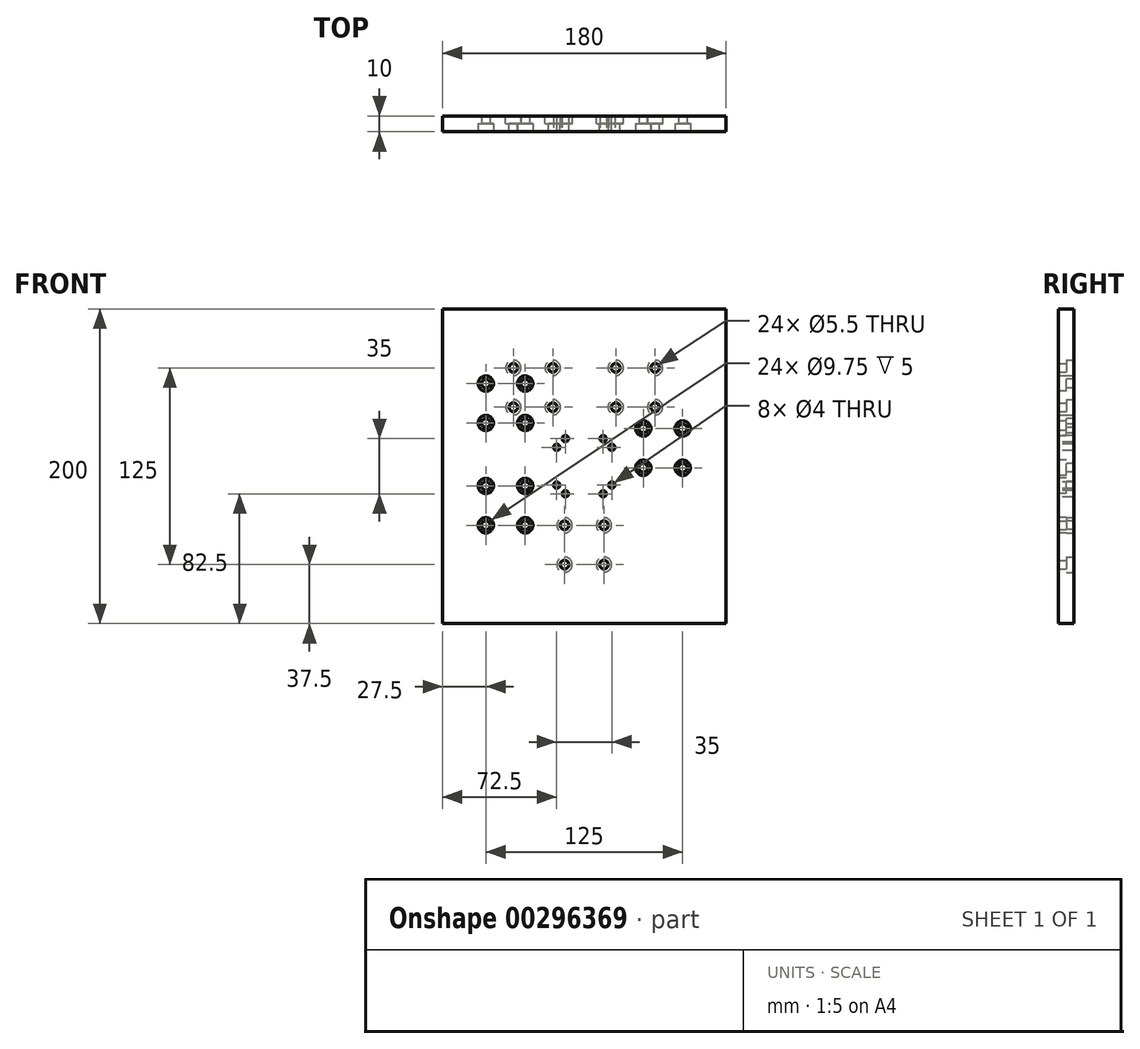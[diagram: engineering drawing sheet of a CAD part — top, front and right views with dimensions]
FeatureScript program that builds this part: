
annotation { "Feature Type Name" : "Feature", "Feature Type Description" : "" }
export const myFeature = defineFeature(function(context is Context, id is Id, definition is map)
    precondition{}
    {
        {
            var Q0;
            Q0=qCreatedBy(makeId("Front.planeOp"),FACE);
            var sketch = newSketch(context, id + "F0", { "sketchPlane" : qUnion([Q0])});
            skLineSegment(sketch, "E0.bottom", {"start": v(90, 100) * mm, "end": v(-90, 100) * mm});
            skLineSegment(sketch, "E0.top", {"start": v(90, -100) * mm, "end": v(-90, -100) * mm});
            skLineSegment(sketch, "E0.left", {"start": v(90, 100) * mm, "end": v(90, -100) * mm});
            skLineSegment(sketch, "E0.right", {"start": v(-90, 100) * mm, "end": v(-90, -100) * mm});
            skPoint(sketch, "E0.middle", {"position": v(0, 0) * mm});
            skLineSegment(sketch, "E1", {"start": v(-90, 50) * mm, "end": v(90, 50) * mm, "construction": true});
            skLineSegment(sketch, "E2", {"start": v(-90, 0) * mm, "end": v(90, 0) * mm, "construction": true});
            skLineSegment(sketch, "E3", {"start": v(-90, -50) * mm, "end": v(90, -50) * mm, "construction": true});
            skLineSegment(sketch, "E4", {"start": v(-32.5, 100) * mm, "end": v(-32.5, 0) * mm, "construction": true});
            skLineSegment(sketch, "E5", {"start": v(0, 100) * mm, "end": v(0, -100) * mm, "construction": true});
            skLineSegment(sketch, "E6", {"start": v(32.5, 100) * mm, "end": v(32.5, 0) * mm, "construction": true});
            skLineSegment(sketch, "E7.0", {"start": v(-45, 60) * mm, "end": v(-45, 0) * mm, "construction": true});
            skLineSegment(sketch, "E8.0", {"start": v(-20, 60) * mm, "end": v(-20, 0) * mm, "construction": true});
            skLineSegment(sketch, "E9.0", {"start": v(20, 60) * mm, "end": v(20, 0) * mm, "construction": true});
            skLineSegment(sketch, "E10.0", {"start": v(45, 60) * mm, "end": v(45, 0) * mm, "construction": true});
            skLineSegment(sketch, "E11.0", {"start": v(-60, 37.5) * mm, "end": v(60, 37.5) * mm, "construction": true});
            skLineSegment(sketch, "E12.0", {"start": v(-60, 62.5) * mm, "end": v(60, 62.5) * mm, "construction": true});
            skLineSegment(sketch, "E13.0", {"start": v(-60, -62.5) * mm, "end": v(60, -62.5) * mm, "construction": true});
            skLineSegment(sketch, "E14.0", {"start": v(-60, -37.5) * mm, "end": v(60, -37.5) * mm, "construction": true});
            skLineSegment(sketch, "E15.trimOffspring", {"start": v(12.5, 0) * mm, "end": v(12.5, -100) * mm, "construction": true});
            skLineSegment(sketch, "E16.trimOffspring", {"start": v(-12.5, 0) * mm, "end": v(-12.5, -100) * mm, "construction": true});
            skPoint(sketch, "E17", {"position": v(-45, 62.5) * mm});
            skPoint(sketch, "E18", {"position": v(-45, 37.5) * mm});
            skPoint(sketch, "E19", {"position": v(-20, 37.5) * mm});
            skPoint(sketch, "E20", {"position": v(-20, 62.5) * mm});
            skPoint(sketch, "E21", {"position": v(20, 62.5) * mm});
            skPoint(sketch, "E22", {"position": v(45, 62.5) * mm});
            skPoint(sketch, "E23", {"position": v(45, 37.5) * mm});
            skPoint(sketch, "E24", {"position": v(20, 37.5) * mm});
            skPoint(sketch, "E25", {"position": v(-12.5, -37.5) * mm});
            skPoint(sketch, "E26", {"position": v(12.5, -37.5) * mm});
            skPoint(sketch, "E27", {"position": v(12.5, -62.5) * mm});
            skPoint(sketch, "E28", {"position": v(-12.5, -62.5) * mm});
            skSolve(sketch);
        }
        {
            var Q0;
            Q0 = qSketchRegion(id + "F0", true);
            extrude(context, id + "F1", {"entities" : qUnion([Q0]), "depth" : 10 * mm});
        }
        {
            var Q0;
            Q0=sQuery(id+"F0.wireOp",VERTEX,"E17");
            var Q1;
            Q1=sQuery(id+"F0.wireOp",VERTEX,"E20");
            var Q2;
            Q2=sQuery(id+"F0.wireOp",VERTEX,"E19");
            var Q3;
            Q3=sQuery(id+"F0.wireOp",VERTEX,"E18");
            var Q4;
            Q4=sQuery(id+"F0.wireOp",VERTEX,"E21");
            var Q5;
            Q5=sQuery(id+"F0.wireOp",VERTEX,"E22");
            var Q6;
            Q6=sQuery(id+"F0.wireOp",VERTEX,"E23");
            var Q7;
            Q7=sQuery(id+"F0.wireOp",VERTEX,"E24");
            var Q8;
            Q8=sQuery(id+"F0.wireOp",VERTEX,"E26");
            var Q9;
            Q9=sQuery(id+"F0.wireOp",VERTEX,"E25");
            var Q10;
            Q10=sQuery(id+"F0.wireOp",VERTEX,"E28");
            var Q11;
            Q11=sQuery(id+"F0.wireOp",VERTEX,"E27");
            var Q12;
            Q12=makeQuery(id+"F1.opExtrude","SWEPT_BODY",BODY,{"disambiguationData":[OSD([sQuery(id+"F0.wireOp",EDGE,"E0.bottom"),sQuery(id+"F0.wireOp",EDGE,"E0.top"),sQuery(id+"F0.wireOp",EDGE,"E0.left"),sQuery(id+"F0.wireOp",EDGE,"E0.right")])]});
            hole(context, id + "F2", {"style" : HoleStyle.C_BORE, "endStyle" : HoleEndStyle.THROUGH, "oppositeDirection" : true, "standardTappedOrClearance" : lookupTablePath({ "standard" : "ISO", "fit" : "Normal", "size" : "M5", "type" : "Clearance" }), "standardBlindInLast" : lookupTablePath({ "fit" : "Standard", "standard" : "ISO", "size" : "M5", "type" : "Clearance" }), "holeDiameter" : 5.5 * mm, "cBoreDiameter" : 9.75 * mm, "cBoreDepth" : 5 * mm, "tappedDepth" : 8 * mm, "tapClearance" : 3, "locations" : qUnion([Q0, Q1, Q2, Q3, Q4, Q5, Q6, Q7, Q8, Q9, Q10, Q11]), "scope" : qUnion([Q12])});
        }
        {
            var Q0;
            Q0=makeQuery(id+"F1.opExtrude","CAP_FACE",FACE,{"disambiguationData":[OSD([sQuery(id+"F0.wireOp",EDGE,"E0.bottom"),sQuery(id+"F0.wireOp",EDGE,"E0.top"),sQuery(id+"F0.wireOp",EDGE,"E0.left"),sQuery(id+"F0.wireOp",EDGE,"E0.right")])],"isStart":false});
            var sketch = newSketch(context, id + "F3", { "sketchPlane" : qUnion([Q0])});
            skLineSegment(sketch, "E29", {"start": v(-50, -100) * mm, "end": v(-50, 100) * mm, "construction": true});
            skLineSegment(sketch, "E30", {"start": v(50, -19.94) * mm, "end": v(50, 100) * mm, "construction": true});
            skLineSegment(sketch, "E31", {"start": v(-90, 0) * mm, "end": v(90, 0) * mm, "construction": true});
            skLineSegment(sketch, "E32", {"start": v(0, -100) * mm, "end": v(0, 100) * mm, "construction": true});
            skLineSegment(sketch, "E33", {"start": v(-90, -25) * mm, "end": v(-10.57, -25) * mm, "construction": true});
            skLineSegment(sketch, "E34", {"start": v(-90, 40) * mm, "end": v(0, 40) * mm, "construction": true});
            skLineSegment(sketch, "E35.0", {"start": v(-60, -37.5) * mm, "end": v(-9.77, -37.5) * mm, "construction": true});
            skLineSegment(sketch, "E36.0", {"start": v(-60, -12.5) * mm, "end": v(-9.77, -12.5) * mm, "construction": true});
            skLineSegment(sketch, "E37.0", {"start": v(-60, 52.5) * mm, "end": v(2.2, 52.5) * mm, "construction": true});
            skLineSegment(sketch, "E38.0", {"start": v(-60, 27.5) * mm, "end": v(0, 27.5) * mm, "construction": true});
            skLineSegment(sketch, "E39.0", {"start": v(62.5, -19.94) * mm, "end": v(62.5, 60) * mm, "construction": true});
            skLineSegment(sketch, "E40.0", {"start": v(37.5, -19.94) * mm, "end": v(37.5, 60) * mm, "construction": true});
            skLineSegment(sketch, "E41.0", {"start": v(-37.5, -60) * mm, "end": v(-37.5, 60) * mm, "construction": true});
            skLineSegment(sketch, "E42.0", {"start": v(-62.5, -60) * mm, "end": v(-62.5, 60) * mm, "construction": true});
            skLineSegment(sketch, "E43.0", {"start": v(-60, 24) * mm, "end": v(60, 24) * mm, "construction": true});
            skLineSegment(sketch, "E44.0", {"start": v(-60, -1) * mm, "end": v(60, -1) * mm, "construction": true});
            skPoint(sketch, "E45", {"position": v(-62.5, -37.5) * mm});
            skPoint(sketch, "E46", {"position": v(-37.5, -37.5) * mm});
            skPoint(sketch, "E47", {"position": v(-37.5, -12.5) * mm});
            skPoint(sketch, "E48", {"position": v(-62.5, -12.5) * mm});
            skPoint(sketch, "E49", {"position": v(-62.5, 52.5) * mm});
            skPoint(sketch, "E50", {"position": v(-37.5, 52.5) * mm});
            skPoint(sketch, "E51", {"position": v(-37.5, 27.5) * mm});
            skPoint(sketch, "E52", {"position": v(-62.5, 27.5) * mm});
            skPoint(sketch, "E53", {"position": v(37.5, -1) * mm});
            skPoint(sketch, "E54", {"position": v(37.5, 24) * mm});
            skPoint(sketch, "E55", {"position": v(62.5, 24) * mm});
            skPoint(sketch, "E56", {"position": v(62.5, -1) * mm});
            skSolve(sketch);
        }
        {
            var Q0;
            Q0=sQuery(id+"F3.wireOp",VERTEX,"E45");
            var Q1;
            Q1=sQuery(id+"F3.wireOp",VERTEX,"E48");
            var Q2;
            Q2=sQuery(id+"F3.wireOp",VERTEX,"E47");
            var Q3;
            Q3=sQuery(id+"F3.wireOp",VERTEX,"E46");
            var Q4;
            Q4=sQuery(id+"F3.wireOp",VERTEX,"E52");
            var Q5;
            Q5=sQuery(id+"F3.wireOp",VERTEX,"E49");
            var Q6;
            Q6=sQuery(id+"F3.wireOp",VERTEX,"E50");
            var Q7;
            Q7=sQuery(id+"F3.wireOp",VERTEX,"E51");
            var Q8;
            Q8=sQuery(id+"F3.wireOp",VERTEX,"E53");
            var Q9;
            Q9=sQuery(id+"F3.wireOp",VERTEX,"E54");
            var Q10;
            Q10=sQuery(id+"F3.wireOp",VERTEX,"E55");
            var Q11;
            Q11=sQuery(id+"F3.wireOp",VERTEX,"E56");
            var Q12;
            Q12=makeQuery(id+"F1.opExtrude","SWEPT_BODY",BODY,{"disambiguationData":[OSD([sQuery(id+"F0.wireOp",EDGE,"E0.bottom"),sQuery(id+"F0.wireOp",EDGE,"E0.top"),sQuery(id+"F0.wireOp",EDGE,"E0.left"),sQuery(id+"F0.wireOp",EDGE,"E0.right")])]});
            hole(context, id + "F4", {"style" : HoleStyle.C_BORE, "endStyle" : HoleEndStyle.THROUGH, "standardTappedOrClearance" : lookupTablePath({ "standard" : "ISO", "fit" : "Normal", "size" : "M5", "type" : "Clearance" }), "standardBlindInLast" : lookupTablePath({ "fit" : "Standard", "standard" : "ISO", "size" : "M5", "type" : "Clearance" }), "holeDiameter" : 5.5 * mm, "cBoreDiameter" : 9.75 * mm, "cBoreDepth" : 5 * mm, "tappedDepth" : 8 * mm, "tapClearance" : 3, "locations" : qUnion([Q0, Q1, Q2, Q3, Q4, Q5, Q6, Q7, Q8, Q9, Q10, Q11]), "scope" : qUnion([Q12])});
        }
        {
            var Q0;
            Q0=makeQuery(id+"F1.opExtrude","CAP_FACE",FACE,{"disambiguationData":[OSD([sQuery(id+"F0.wireOp",EDGE,"E0.bottom"),sQuery(id+"F0.wireOp",EDGE,"E0.top"),sQuery(id+"F0.wireOp",EDGE,"E0.left"),sQuery(id+"F0.wireOp",EDGE,"E0.right")])],"isStart":false});
            var sketch = newSketch(context, id + "F5", { "sketchPlane" : qUnion([Q0])});
            skLineSegment(sketch, "E57", {"start": v(-62.5, 27.5) * mm, "end": v(-62.5, -12.5) * mm, "construction": true});
            skLineSegment(sketch, "E58", {"start": v(-17.5, 12) * mm, "end": v(-17.5, -12) * mm, "construction": true});
            skLineSegment(sketch, "E59", {"start": v(17.5, 12) * mm, "end": v(17.5, -12) * mm, "construction": true});
            skPoint(sketch, "E60", {"position": v(-17.5, 12) * mm});
            skPoint(sketch, "E61", {"position": v(-17.5, -12) * mm});
            skPoint(sketch, "E62", {"position": v(17.5, -12) * mm});
            skPoint(sketch, "E63", {"position": v(17.5, 12) * mm});
            skLineSegment(sketch, "E64", {"start": v(-20, 37.5) * mm, "end": v(20, 37.5) * mm, "construction": true});
            skLineSegment(sketch, "E65", {"start": v(-17.5, 12) * mm, "end": v(17.5, 12) * mm, "construction": true});
            skLineSegment(sketch, "E66", {"start": v(-17.5, -12) * mm, "end": v(17.5, -12) * mm, "construction": true});
            skLineSegment(sketch, "E67.bottom", {"start": v(-12, 17.5) * mm, "end": v(12, 17.5) * mm, "construction": true});
            skLineSegment(sketch, "E67.top", {"start": v(-12, -17.5) * mm, "end": v(12, -17.5) * mm, "construction": true});
            skLineSegment(sketch, "E67.left", {"start": v(-12, 17.5) * mm, "end": v(-12, -17.5) * mm, "construction": true});
            skLineSegment(sketch, "E67.right", {"start": v(12, 17.5) * mm, "end": v(12, -17.5) * mm, "construction": true});
            skSolve(sketch);
        }
        {
            var Q0;
            Q0=sQuery(id+"F5.wireOp",VERTEX,"E60");
            var Q1;
            Q1=sQuery(id+"F5.wireOp",VERTEX,"E61");
            var Q2;
            Q2=sQuery(id+"F5.wireOp",VERTEX,"E62");
            var Q3;
            Q3=sQuery(id+"F5.wireOp",VERTEX,"E63");
            var Q4;
            Q4=sQuery(id+"F5.wireOp",VERTEX,"E67.left.start");
            var Q5;
            Q5=sQuery(id+"F5.wireOp",VERTEX,"E67.right.start");
            var Q6;
            Q6=sQuery(id+"F5.wireOp",VERTEX,"E67.right.end");
            var Q7;
            Q7=sQuery(id+"F5.wireOp",VERTEX,"E67.top.start");
            var Q8;
            Q8=makeQuery(id+"F1.opExtrude","SWEPT_BODY",BODY,{"disambiguationData":[OSD([sQuery(id+"F0.wireOp",EDGE,"E0.bottom"),sQuery(id+"F0.wireOp",EDGE,"E0.top"),sQuery(id+"F0.wireOp",EDGE,"E0.left"),sQuery(id+"F0.wireOp",EDGE,"E0.right")])]});
            hole(context, id + "F6", {"style" : HoleStyle.SIMPLE, "endStyle" : HoleEndStyle.THROUGH, "standardTappedOrClearance" : lookupTablePath({ "standard" : "ISO", "engagement" : "75%", "pitch" : "1 mm", "size" : "M5", "type" : "Tapped" }), "standardBlindInLast" : lookupTablePath({ "standard" : "ISO", "engagement" : "75%", "pitch" : "1 mm", "size" : "M5", "type" : "Tapped" }), "holeDiameter" : 4 * mm, "showTappedDepth" : true, "tappedDepth" : 9.6 * mm, "tapClearance" : 3, "locations" : qUnion([Q0, Q1, Q2, Q3, Q4, Q5, Q6, Q7]), "scope" : qUnion([Q8])});
        }
    });
